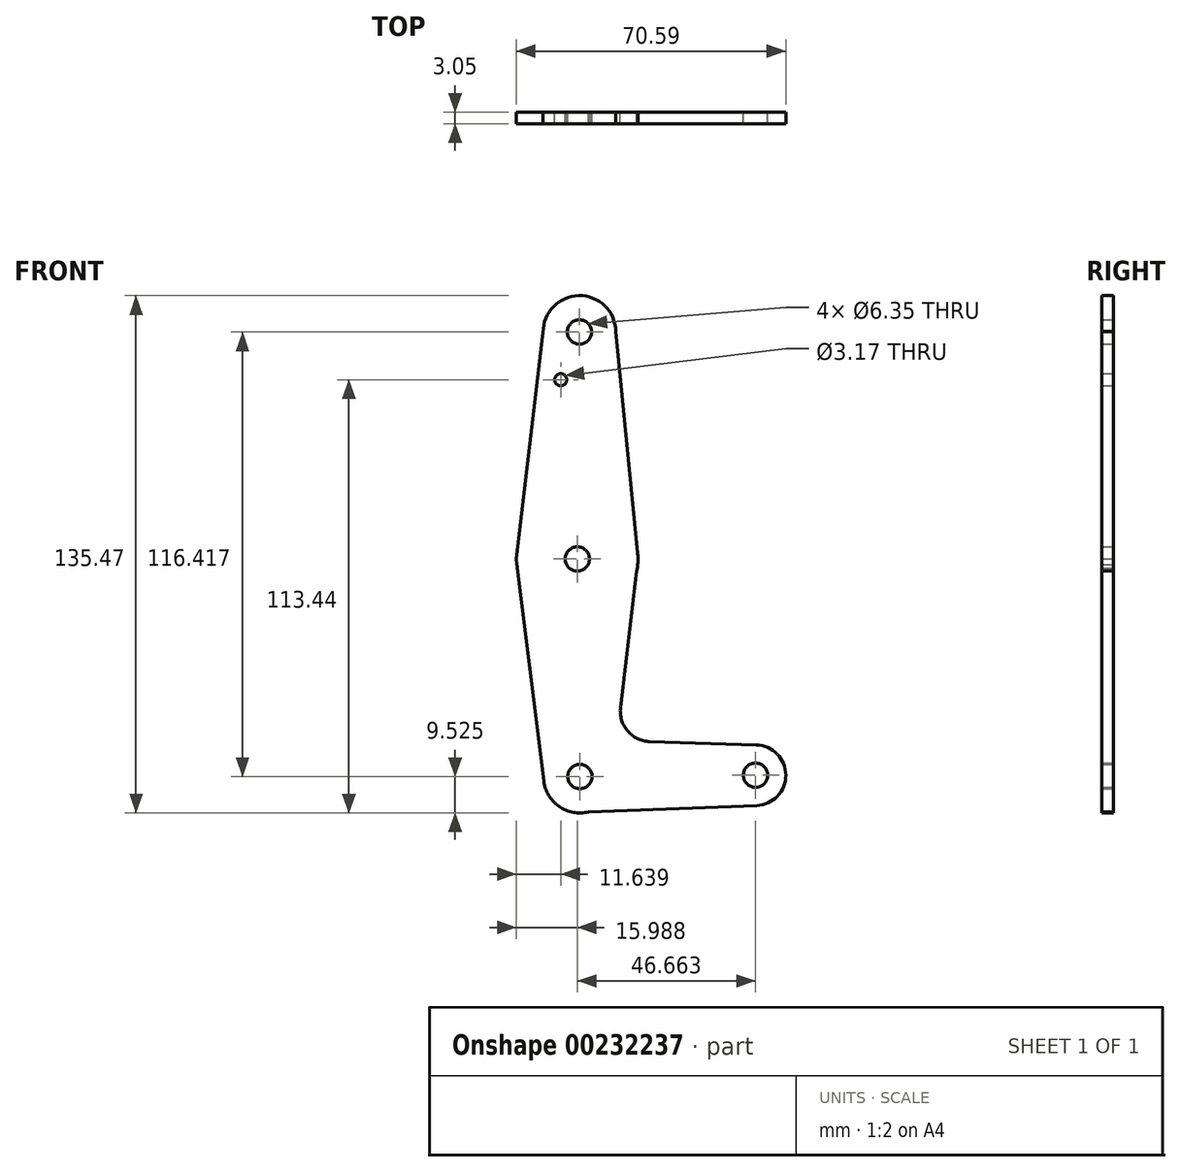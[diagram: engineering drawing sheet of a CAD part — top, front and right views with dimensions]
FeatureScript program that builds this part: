
annotation { "Feature Type Name" : "Feature", "Feature Type Description" : "" }
export const myFeature = defineFeature(function(context is Context, id is Id, definition is map)
    precondition{}
    {
        {
            var Q0;
            Q0=qCreatedBy(makeId("Front.planeOp"),FACE);
            var sketch = newSketch(context, id + "F0", { "sketchPlane" : qUnion([Q0])});
            skCircle(sketch, "E0", {"center": v(-34.5, 0.02) * mm, "radius": 15.88 * mm});
            skCircle(sketch, "E1", {"center": v(-33.93, 59.46) * mm, "radius": 9.53 * mm});
            skCircle(sketch, "E2", {"center": v(12.16, -56.62) * mm, "radius": 7.94 * mm});
            skCircle(sketch, "E3", {"center": v(-33.84, -56.96) * mm, "radius": 9.53 * mm});
            skLineSegment(sketch, "E4", {"start": v(-34.08, -54.74) * mm, "end": v(-34.08, 59.56) * mm});
            skLineSegment(sketch, "E5", {"start": v(-34.08, -54.74) * mm, "end": v(10.37, -54.74) * mm});
            skLineSegment(sketch, "E6", {"start": v(-43.46, 59.35) * mm, "end": v(-50.5, 0) * mm});
            skLineSegment(sketch, "E7", {"start": v(-24.4, 59.65) * mm, "end": v(-18.55, 0) * mm});
            skLineSegment(sketch, "E8", {"start": v(-50.5, 0) * mm, "end": v(-43.29, -58.13) * mm});
            skLineSegment(sketch, "E9", {"start": v(-18.94, -3.13) * mm, "end": v(-23.19, -38.92) * mm});
            skLineSegment(sketch, "E10", {"start": v(-15.54, -47.8) * mm, "end": v(12.41, -48.69) * mm});
            skLineSegment(sketch, "E11", {"start": v(-31.56, -66.2) * mm, "end": v(12.46, -64.55) * mm});
            skCircle(sketch, "E12", {"center": v(-33.93, 59.46) * mm, "radius": 3.18 * mm});
            skCircle(sketch, "E13", {"center": v(-34.5, 0.02) * mm, "radius": 3.18 * mm});
            skCircle(sketch, "E14", {"center": v(-33.84, -56.96) * mm, "radius": 3.18 * mm});
            skCircle(sketch, "E15", {"center": v(12.16, -56.62) * mm, "radius": 3.18 * mm});
            skArc(sketch, "E16.filletArc", {"start": v(-23.19, -38.92) * mm, "mid": v(-21.32, -45.04) * mm, "end": v(-15.54, -47.8) * mm});
            skCircle(sketch, "E17", {"center": v(-38.85, 46.96) * mm, "radius": 1.59 * mm});
            skSolve(sketch);
        }
        {
            var Q0;
            Q0 = qSketchRegion(id + "F0", true);
            var Q1;
            {var subQ0=sQuery(id+"F0.wireOp",EDGE,"E4");var subQ1=sQuery(id+"F0.wireOp",EDGE,"E3");var subQ2=makeQuery(id+"F0.imprint","INTERSECT",VERTEX,{"derivedFrom":[subQ1,subQ0]});Q1=makeQuery(id+"F0.imprint","IMPRINT",FACE,{"disambiguationData":[TD([[makeQuery(id+"F0.imprint","IMPRINT",EDGE,{"disambiguationData":[TD([[subQ2,1.0]])],"derivedFrom":subQ1}),1.0]])]});}
            extrude(context, id + "F1", {"entities" : qUnion([Q0, Q1]), "depth" : 3.05 * mm});
        }
    });
